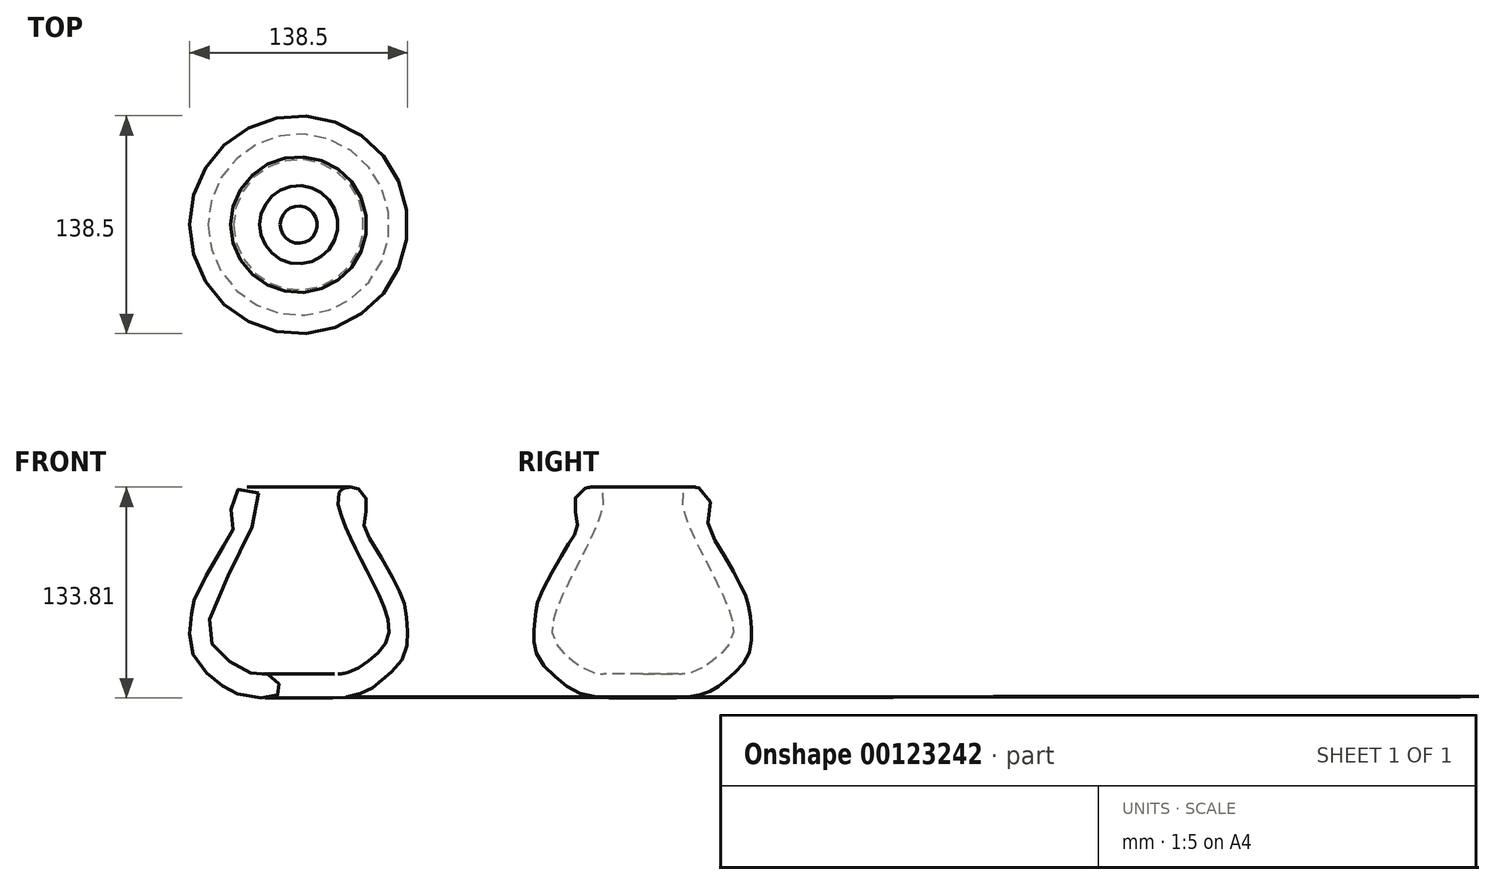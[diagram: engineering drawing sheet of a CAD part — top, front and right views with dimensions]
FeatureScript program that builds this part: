
annotation { "Feature Type Name" : "Feature", "Feature Type Description" : "" }
export const myFeature = defineFeature(function(context is Context, id is Id, definition is map)
    precondition{}
    {
        {
            var Q0;
            Q0=qCreatedBy(makeId("Front.planeOp"),FACE);
            var sketch = newSketch(context, id + "F0", { "sketchPlane" : qUnion([Q0])});
            skLineSegment(sketch, "E0", {"start": v(0, 75.74) * mm, "end": v(0, -102.74) * mm, "construction": true});
            skFitSpline(sketch, "E1", {"points": [v(-25.61, 61.85) * mm, v(-56.32, -16.84) * mm, v(-50.4, -39.48) * mm, v(-29.83, -52.6) * mm, v(-18.26, -53.62) * mm, v(-12.34, -60.3) * mm, v(-12.6, -65.7) * mm, v(-20.83, -68.28) * mm, v(-41.66, -64.68) * mm, v(-51.18, -58.5) * mm, v(-65.83, -43.59) * mm, v(-69.18, -25.85) * mm, v(-67.63, -11.96) * mm, v(-65.06, -2.96) * mm, v(-44.75, 33.3) * mm, v(-41.4, 41.28) * mm, v(-41.25, 61.85) * mm, v(-25.61, 61.85) * mm]});
            skSolve(sketch);
        }
        {
            var Q0;
            Q0=makeQuery(id+"F0.imprint","IMPRINT",FACE,{"disambiguationData":[TD([[makeQuery(id+"F0.imprint","IMPRINT",EDGE,{"derivedFrom":sQuery(id+"F0.wireOp",EDGE,"E1")}),-1.0]])]});
            var Q1;
            Q1=sQuery(id+"F0.wireOp",EDGE,"E0");
            revolve(context, id + "F1", {"entities" : qUnion([Q0]), "axis" : qUnion([Q1]), "revolveType" : RevolveType.FULL});
        }
    });
